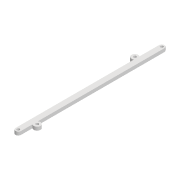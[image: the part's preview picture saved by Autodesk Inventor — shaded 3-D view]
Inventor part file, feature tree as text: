
AUTODESK INVENTOR PART (.ipt)
format: ipt  version: 2022 (Build 260153000, 153)  size: 103,936 bytes
history: native  units: mm
features: extrude x1, sketch x1
ambient origin geometry x8: Origin, YZ Plane, XZ Plane, XY Plane, X Axis, Y Axis, Z Axis, Center Point
bodies: Solid1 (feature_tree)
feature tree (2):
  extrude  "Extrusion1"  Depth=8.0mm
  sketch  "Sketch1"  dims[d0=210.0mm d1=8.0mm d2=4.2mm d3=4.2mm d4=5.0mm d5=0.0mm d6=4.2mm d7=4.2mm d8=3.0mm d9=3.0mm d10=10.0mm d11=10.0mm d12=21.0mm d13=182.0mm]
